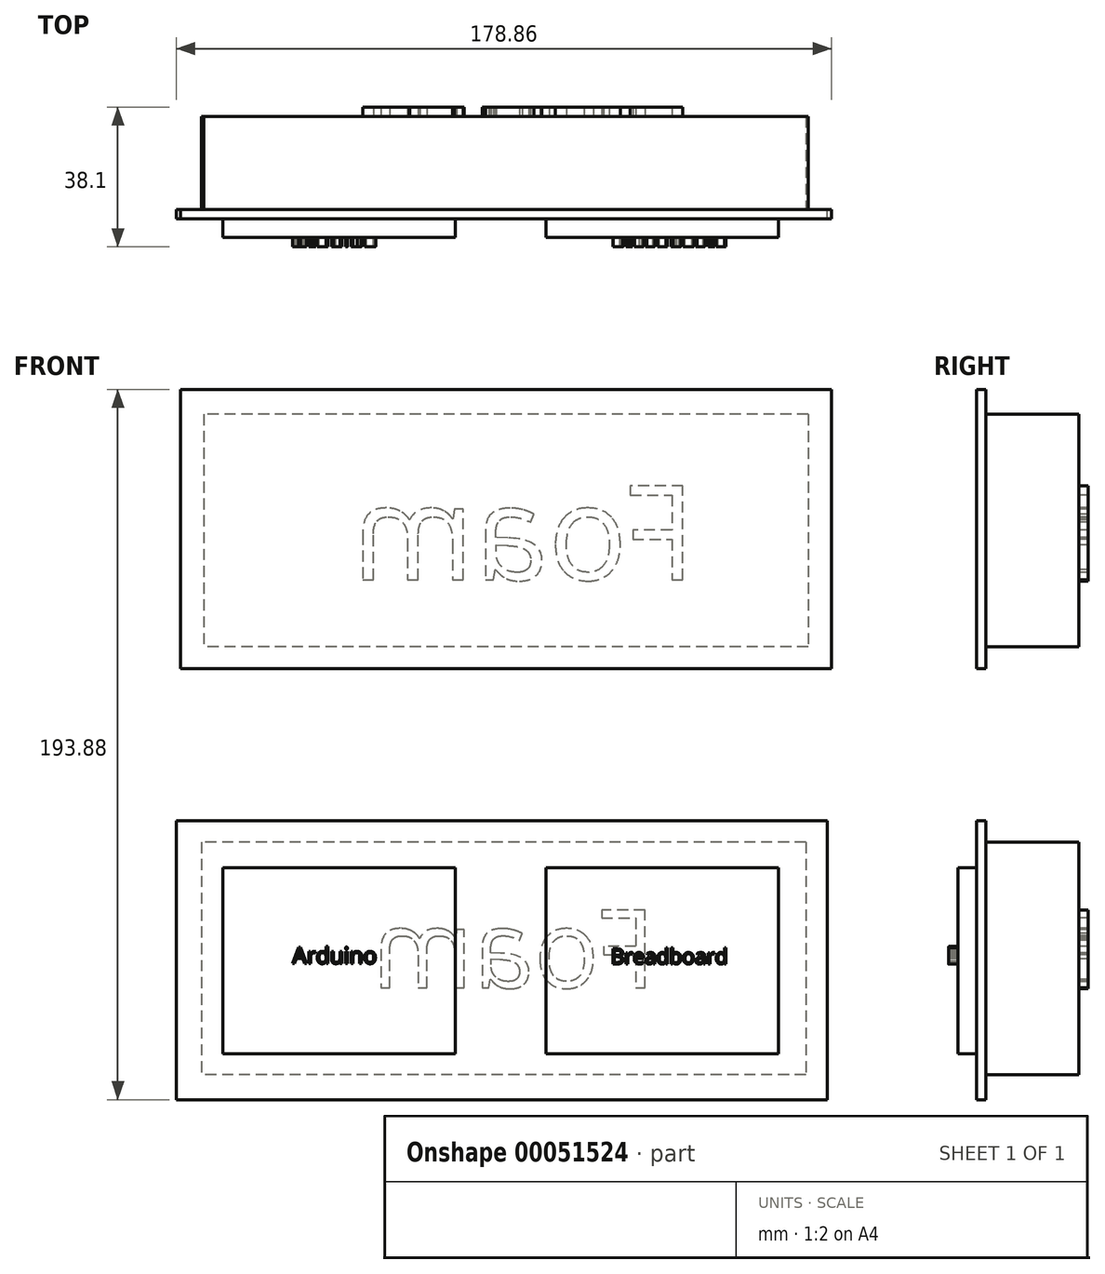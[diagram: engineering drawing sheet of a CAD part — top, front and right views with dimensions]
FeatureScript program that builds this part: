
annotation { "Feature Type Name" : "Feature", "Feature Type Description" : "" }
export const myFeature = defineFeature(function(context is Context, id is Id, definition is map)
    precondition{}
    {
        {
            var Q0;
            Q0=qCreatedBy(makeId("Front.planeOp"),FACE);
            var sketch = newSketch(context, id + "F0", { "sketchPlane" : qUnion([Q0])});
            skLineSegment(sketch, "E0.bottom", {"start": v(-88.7, 59.25) * mm, "end": v(89.1, 59.25) * mm});
            skLineSegment(sketch, "E0.top", {"start": v(-88.7, -16.95) * mm, "end": v(89.1, -16.95) * mm});
            skLineSegment(sketch, "E0.left", {"start": v(-88.7, 59.25) * mm, "end": v(-88.7, -16.95) * mm});
            skLineSegment(sketch, "E0.right", {"start": v(89.1, 59.25) * mm, "end": v(89.1, -16.95) * mm});
            skSolve(sketch);
        }
        {
            var Q0;
            Q0=makeQuery(id+"F0.imprint","IMPRINT",FACE,{"disambiguationData":[TD([[makeQuery(id+"F0.imprint","IMPRINT",EDGE,{"derivedFrom":sQuery(id+"F0.wireOp",EDGE,"E0.bottom")}),-1.0]])]});
            extrude(context, id + "F1", {"entities" : qUnion([Q0]), "depth" : 2.54 * mm});
        }
        {
            var Q0;
            Q0=makeQuery(id+"F1.opExtrude","CAP_FACE",FACE,{"disambiguationData":[OSD([sQuery(id+"F0.wireOp",EDGE,"E0.bottom"),sQuery(id+"F0.wireOp",EDGE,"E0.top"),sQuery(id+"F0.wireOp",EDGE,"E0.left"),sQuery(id+"F0.wireOp",EDGE,"E0.right")])],"isStart":false});
            var sketch = newSketch(context, id + "F2", { "sketchPlane" : qUnion([Q0])});
            skLineSegment(sketch, "E1.bottom", {"start": v(-76, 46.35) * mm, "end": v(-12.5, 46.35) * mm});
            skLineSegment(sketch, "E1.top", {"start": v(-76, -4.45) * mm, "end": v(-12.5, -4.45) * mm});
            skLineSegment(sketch, "E1.left", {"start": v(-76, 46.35) * mm, "end": v(-76, -4.45) * mm});
            skLineSegment(sketch, "E1.right", {"start": v(-12.5, 46.35) * mm, "end": v(-12.5, -4.45) * mm});
            skLineSegment(sketch, "E2.right", {"start": v(75.77, 46.43) * mm, "end": v(75.77, -4.37) * mm});
            skLineSegment(sketch, "E2.bottom", {"start": v(12.27, 46.43) * mm, "end": v(75.77, 46.43) * mm});
            skLineSegment(sketch, "E2.left", {"start": v(12.27, 46.43) * mm, "end": v(12.27, -4.37) * mm});
            skLineSegment(sketch, "E2.top", {"start": v(12.27, -4.37) * mm, "end": v(75.77, -4.37) * mm});
            skPoint(sketch, "E3", {"position": v(-76, 46.35) * mm});
            skPoint(sketch, "E4", {"position": v(-88.7, 46.73) * mm});
            skPoint(sketch, "E5", {"position": v(89.1, 45.52) * mm});
            skPoint(sketch, "E6", {"position": v(76.4, 46.13) * mm});
            skSolve(sketch);
        }
        {
            var Q0;
            Q0=makeQuery(id+"F2.imprint","IMPRINT",FACE,{"disambiguationData":[TD([[makeQuery(id+"F2.imprint","IMPRINT",EDGE,{"derivedFrom":sQuery(id+"F2.wireOp",EDGE,"E1.bottom")}),-1.0]])]});
            var Q1;
            Q1=makeQuery(id+"F2.imprint","IMPRINT",FACE,{"disambiguationData":[TD([[makeQuery(id+"F2.imprint","IMPRINT",EDGE,{"derivedFrom":sQuery(id+"F2.wireOp",EDGE,"E2.right")}),-1.0]])]});
            extrude(context, id + "F3", {"entities" : qUnion([Q0, Q1]), "operationType" : NewBodyOperationType.ADD, "depth" : 5.08 * mm});
        }
        {
            var Q0;
            Q0=makeQuery(id+"F3.opExtrude","CAP_FACE",FACE,{"disambiguationData":[OSD([sQuery(id+"F2.wireOp",EDGE,"E1.bottom"),sQuery(id+"F2.wireOp",EDGE,"E1.top"),sQuery(id+"F2.wireOp",EDGE,"E1.left"),sQuery(id+"F2.wireOp",EDGE,"E1.right")])],"isStart":false});
            var sketch = newSketch(context, id + "F4", { "sketchPlane" : qUnion([Q0])});
            skText(sketch, "E7", { "text": "Arduino", "fontName": "OpenSans-Regular.ttf"});
            skText(sketch, "E8", { "text": "Breadboard ", "fontName": "OpenSans-Regular.ttf"});
            const initialGuessF4  = {"E7": [-0.05703, 0.0202, 1, 0, 0.00444], "E8": [0.0299, 0.02012, 1, 0, 0.00413]};
            skSetInitialGuess(sketch, initialGuessF4);
            skSolve(sketch);
        }
        {
            var Q0;
            Q0 = qSketchRegion(id + "F4", true);
            extrude(context, id + "F5", {"entities" : qUnion([Q0]), "operationType" : NewBodyOperationType.ADD, "depth" : 2.54 * mm});
        }
        {
            var Q0;
            Q0=makeQuery(id+"F1.opExtrude","CAP_FACE",FACE,{"disambiguationData":[OSD([sQuery(id+"F0.wireOp",EDGE,"E0.bottom"),sQuery(id+"F0.wireOp",EDGE,"E0.top"),sQuery(id+"F0.wireOp",EDGE,"E0.left"),sQuery(id+"F0.wireOp",EDGE,"E0.right")])],"isStart":true});
            var sketch = newSketch(context, id + "F6", { "sketchPlane" : qUnion([Q0])});
            skLineSegment(sketch, "E9.bottom", {"start": v(-83.18, 53.34) * mm, "end": v(81.92, 53.34) * mm});
            skLineSegment(sketch, "E9.top", {"start": v(-83.18, -10.16) * mm, "end": v(81.92, -10.16) * mm});
            skLineSegment(sketch, "E9.left", {"start": v(-83.18, 53.34) * mm, "end": v(-83.18, -10.16) * mm});
            skLineSegment(sketch, "E9.right", {"start": v(81.92, 53.34) * mm, "end": v(81.92, -10.16) * mm});
            skSolve(sketch);
        }
        {
            var Q0;
            Q0=makeQuery(id+"F6.imprint","IMPRINT",FACE,{"disambiguationData":[TD([[makeQuery(id+"F6.imprint","IMPRINT",EDGE,{"derivedFrom":sQuery(id+"F6.wireOp",EDGE,"E9.bottom")}),-1.0]])]});
            extrude(context, id + "F7", {"entities" : qUnion([Q0]), "operationType" : NewBodyOperationType.ADD, "depth" : 25.4 * mm});
        }
        {
            var Q0;
            Q0=makeQuery(id+"F7.opExtrude","CAP_FACE",FACE,{"disambiguationData":[OSD([sQuery(id+"F6.wireOp",EDGE,"E9.bottom"),sQuery(id+"F6.wireOp",EDGE,"E9.top"),sQuery(id+"F6.wireOp",EDGE,"E9.left"),sQuery(id+"F6.wireOp",EDGE,"E9.right")])],"isStart":false});
            var sketch = newSketch(context, id + "F8", { "sketchPlane" : qUnion([Q0])});
            skText(sketch, "E10", { "text": "Foam", "fontName": "OpenSans-Regular.ttf"});
            const initialGuessF8  = {"E10": [-0.04216, 0.01362, 1, 0, 0.02139]};
            skSetInitialGuess(sketch, initialGuessF8);
            skSolve(sketch);
        }
        {
            var Q0;
            Q0 = qSketchRegion(id + "F8", true);
            extrude(context, id + "F9", {"entities" : qUnion([Q0]), "operationType" : NewBodyOperationType.ADD, "depth" : 2.54 * mm});
        }
        {
            var Q0;
            Q0=qCreatedBy(makeId("Front.planeOp"),FACE);
            var sketch = newSketch(context, id + "F10", { "sketchPlane" : qUnion([Q0])});
            skLineSegment(sketch, "E11.bottom", {"start": v(-87.65, 100.73) * mm, "end": v(90.15, 100.73) * mm});
            skLineSegment(sketch, "E11.top", {"start": v(-87.65, 176.93) * mm, "end": v(90.15, 176.93) * mm});
            skLineSegment(sketch, "E11.left", {"start": v(-87.65, 100.73) * mm, "end": v(-87.65, 176.93) * mm});
            skLineSegment(sketch, "E11.right", {"start": v(90.15, 100.73) * mm, "end": v(90.15, 176.93) * mm});
            skSolve(sketch);
        }
        {
            var Q0;
            Q0=makeQuery(id+"F10.imprint","IMPRINT",FACE,{"disambiguationData":[TD([[makeQuery(id+"F10.imprint","IMPRINT",EDGE,{"derivedFrom":sQuery(id+"F10.wireOp",EDGE,"E11.bottom")}),1.0]])]});
            extrude(context, id + "F11", {"entities" : qUnion([Q0]), "depth" : 2.54 * mm});
        }
        {
            var Q0;
            Q0=makeQuery(id+"F11.opExtrude","CAP_FACE",FACE,{"disambiguationData":[OSD([sQuery(id+"F10.wireOp",EDGE,"E11.bottom"),sQuery(id+"F10.wireOp",EDGE,"E11.top"),sQuery(id+"F10.wireOp",EDGE,"E11.left"),sQuery(id+"F10.wireOp",EDGE,"E11.right")])],"isStart":true});
            var sketch = newSketch(context, id + "F12", { "sketchPlane" : qUnion([Q0])});
            skLineSegment(sketch, "E12.bottom", {"start": v(-83.82, 170.2) * mm, "end": v(81.28, 170.2) * mm});
            skLineSegment(sketch, "E12.top", {"start": v(-83.82, 106.7) * mm, "end": v(81.28, 106.7) * mm});
            skLineSegment(sketch, "E12.left", {"start": v(-83.82, 170.2) * mm, "end": v(-83.82, 106.7) * mm});
            skLineSegment(sketch, "E12.right", {"start": v(81.28, 170.2) * mm, "end": v(81.28, 106.7) * mm});
            skSolve(sketch);
        }
        {
            var Q0;
            Q0=makeQuery(id+"F12.imprint","IMPRINT",FACE,{"disambiguationData":[TD([[makeQuery(id+"F12.imprint","IMPRINT",EDGE,{"derivedFrom":sQuery(id+"F12.wireOp",EDGE,"E12.bottom")}),-1.0]])]});
            extrude(context, id + "F13", {"entities" : qUnion([Q0]), "operationType" : NewBodyOperationType.ADD, "depth" : 25.4 * mm});
        }
        {
            var Q0;
            Q0=makeQuery(id+"F13.opExtrude","CAP_FACE",FACE,{"disambiguationData":[OSD([sQuery(id+"F12.wireOp",EDGE,"E12.bottom"),sQuery(id+"F12.wireOp",EDGE,"E12.top"),sQuery(id+"F12.wireOp",EDGE,"E12.left"),sQuery(id+"F12.wireOp",EDGE,"E12.right")])],"isStart":false});
            var sketch = newSketch(context, id + "F14", { "sketchPlane" : qUnion([Q0])});
            skText(sketch, "E13", { "text": "Foam\n", "fontName": "OpenSans-Regular.ttf"});
            const initialGuessF14  = {"E13": [-0.05312, 0.12498, 1, 0, 0.02594]};
            skSetInitialGuess(sketch, initialGuessF14);
            skSolve(sketch);
        }
        {
            var Q0;
            Q0 = qSketchRegion(id + "F14", true);
            extrude(context, id + "F15", {"entities" : qUnion([Q0]), "operationType" : NewBodyOperationType.ADD, "depth" : 2.54 * mm});
        }
        {
            var Q0;
            Q0=makeQuery(id+"F6.imprint","IMPRINT",FACE,{"disambiguationData":[TD([[makeQuery(id+"F6.imprint","IMPRINT",EDGE,{"derivedFrom":sQuery(id+"F6.wireOp",EDGE,"E9.bottom")}),-1.0]])]});
            extrude(context, id + "F16", {"entities" : qUnion([Q0]), "operationType" : NewBodyOperationType.ADD, "depth" : 25.4 * mm});
        }
    });
